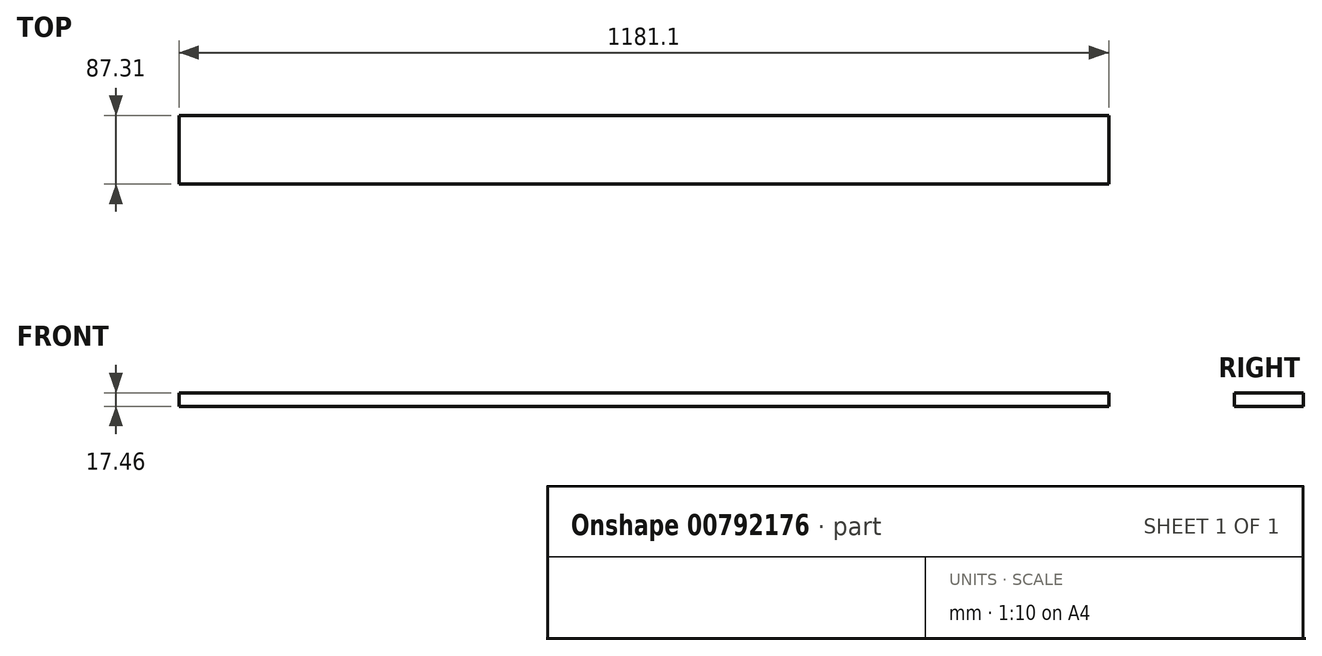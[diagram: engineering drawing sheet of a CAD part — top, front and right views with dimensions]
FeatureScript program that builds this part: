
annotation { "Feature Type Name" : "Feature", "Feature Type Description" : "" }
export const myFeature = defineFeature(function(context is Context, id is Id, definition is map)
    precondition{}
    {
        {
            var Q0;
            Q0=qCreatedBy(makeId("Top.planeOp"),FACE);
            var sketch = newSketch(context, id + "F0", { "sketchPlane" : qUnion([Q0])});
            skLineSegment(sketch, "E0.bottom", {"start": v(0, 0) * mm, "end": v(-1181.1, 0) * mm});
            skLineSegment(sketch, "E0.top", {"start": v(0, 87.31) * mm, "end": v(-1181.1, 87.31) * mm});
            skLineSegment(sketch, "E0.left", {"start": v(0, 0) * mm, "end": v(0, 87.31) * mm});
            skLineSegment(sketch, "E0.right", {"start": v(-1181.1, 0) * mm, "end": v(-1181.1, 87.31) * mm});
            skSolve(sketch);
        }
        {
            var Q0;
            Q0 = qSketchRegion(id + "F0", true);
            extrude(context, id + "F1", {"entities" : qUnion([Q0]), "depth" : 17.46 * mm, "offsetDistance" : 25.4 * mm});
        }
    });
